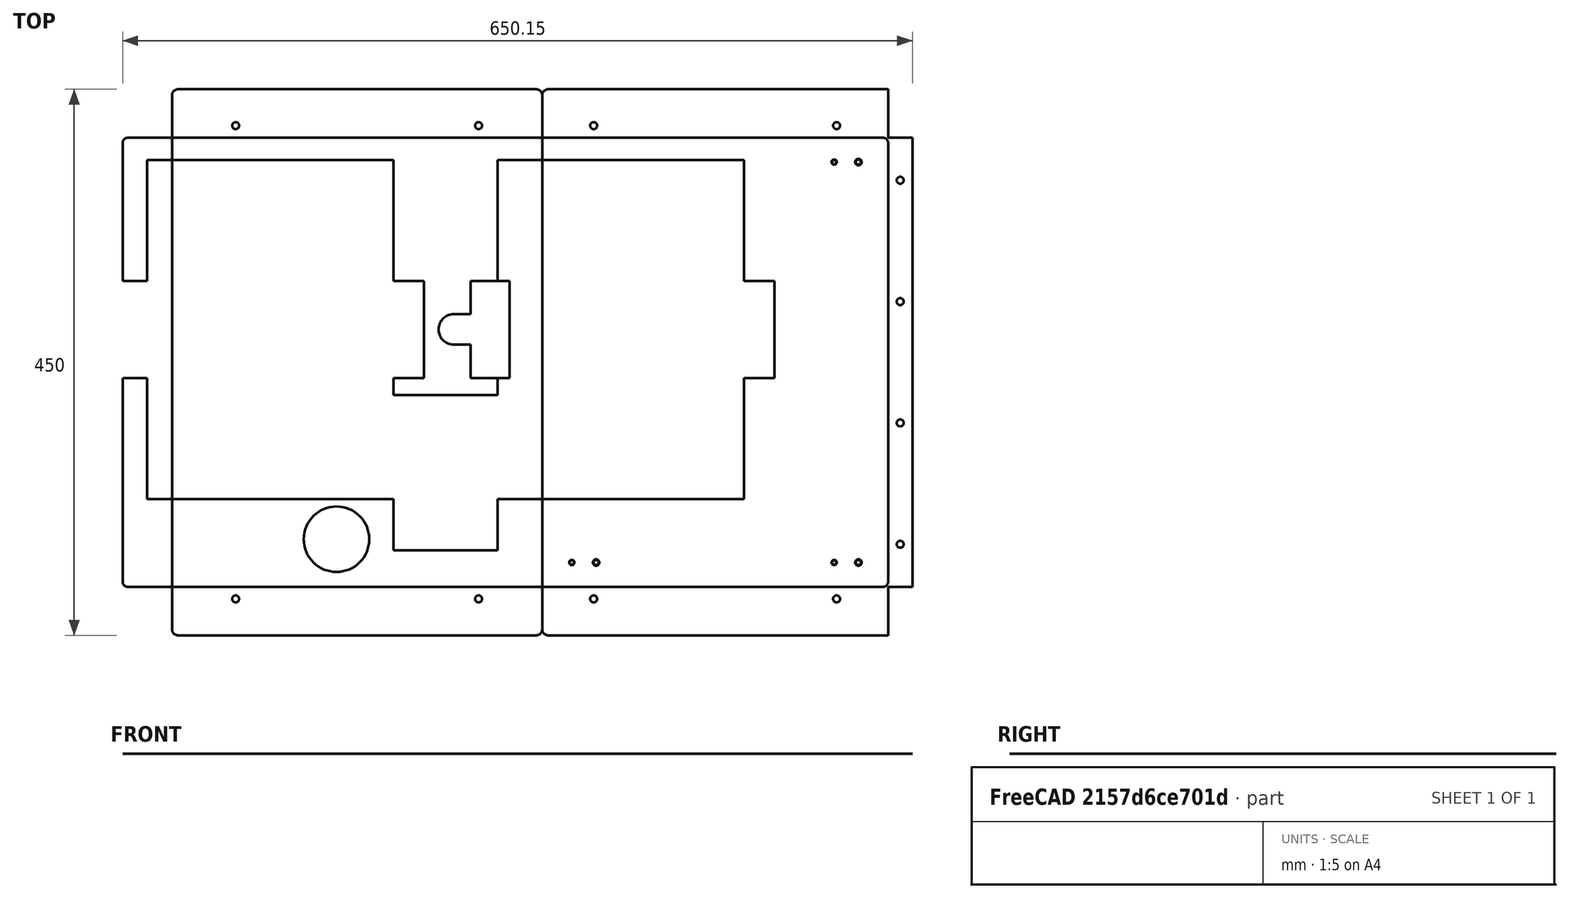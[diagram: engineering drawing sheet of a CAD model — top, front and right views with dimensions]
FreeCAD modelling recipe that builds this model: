
FCSTD DOCUMENT  (FreeCAD 0.18R14715 (Git))
Label: worksurface
License: All rights reserved
LicenseURL: http://en.wikipedia.org/wiki/All_rights_reserved
objects: Part::Feature×5, App::DocumentObjectGroup×5, Part::Part2DObjectPython×4, Spreadsheet::Sheet×1, App::FeaturePython×1, Part::FeaturePython×1
note: 10 computed .brp shape members not serialized (recipe doc carries the construction recipe); baked Part::Feature solids carry a one-line shape summary decoded from their .brp

FEATURE [Spreadsheet::Sheet] Spreadsheet  label="params"
  cells = A1=Name; B1=Value; C1=Notes; A2=sheet_width; B2(sheet_width)==12in; A3=sheet_length; B3(sheet_length)==24in; A4=y_rail_length; B4(y_rail_length)==370mm; A5=extrusion_unit_width; B5(extrusion_unit_width)==20mm; A6=mounting_hole_diam; B6(mounting_hole_diam)==5.75mm; A7=x_rail_hole_spacing; B7(x_rail_hole_spacing)==200mm; A8=y_rail_hole_spacing; B8(y_rail_hole_spacing)==100mm; A9=holes_offset_by; B9(holes_offset_by)==0mm; C9=It seems I made a mistake when this seemed nonzero earlier.; A10=x_rail_length; B10(x_rail_length)==1120mm; A11=flyplate_length; B11(flyplate_length)==85.5mm; A12=flyplate_height; B12(flyplate_height)==128mm; A13=morgue_diam; B13(morgue_diam)==54mm; C13=Smaller part of petri dish. Scintillation vial won't work, because it's too tall, at least with my current (alternate) Z-slides.; A14=dsub_height; B14(dsub_height)==32mm; C14=Adds a significant amount of space so you can grab it through the hole with your fingers.; A15=dsub_length; B15(dsub_length)==80mm; A16=chamber_bottom_to_dsub_mid; B16(chamber_bottom_to_dsub_mid)==6mm; C16=Clearance needs to account for PCB holes being offset a little from bottom, depending on chamber version.; A17=alignment_plate_min_thickness; B17(alignment_plate_min_thickness)==12.199999999999999mm; C17=So guide acrylic doesn't break so easily.  Divided total remaining space by 3.; A18=v1_chamber_length; B18(v1_chamber_length)==279.39999999999998mm; C18=TODO make above clearance larger if I have space; A19=v1_chamber_height; B19(v1_chamber_height)==203mm; A20=v1_nub_length; B20(v1_nub_length)==80mm; C20=Centered on chamber.; A21=v1_nub_height; B21(v1_nub_height)==25mm; C21=TODO how to accomodate both chambers? just use nub on top for v1? possible?; A22=v2_chamber_length; B22(v2_chamber_length)==279.39999999999998mm; C22=v2 chamber doesn't have the motor mounting nub v1 has.; A23=v2_chamber_height; B23(v2_chamber_height)==203mm; A24=cable_passthru_diam; B24(cable_passthru_diam)==25mm; C24=TODO have everything automatically evenly spaced (& automatically put as many flyplates in as possible?); A25=dsub_to_passthru; B25(dsub_to_passthru)==30mm; C25=Kind of long, so I hopefully won't have to bend cable too much when (dis)connecting.; C26=TODO flyplate orientation marks? minimum clearance for auto number as above; A27=primary_alignment_hole_diam; B27(primary_alignment_hole_diam)==0.13600000000000001in; A28=secondary_alignment_hole_diam; B28(secondary_alignment_hole_diam)==4.2000000000000002mm; C28=TODO how to basically make array of 3 of something, on a (right) triangle?; A29=primary_alignment_hole_upper_diam; B29(primary_alignment_hole_upper_diam)==4.2999999999999998mm; C29=Measured at bottom of taper pin (widest part).; A30=secondary_alignment_hole_upper_diam; B30(secondary_alignment_hole_upper_diam)==5.2999999999999998mm; C31=TODO TODO passthroughs for flow from below; C32=TODO TODO make space for more behavior chambers, and just support mounting onto multiple slats below?; C33=TODO TODO TODO consider reorienting chamber chambers,  particularly if doing above, to pack more in; C34=TODO how many cable passthroughs do I want?; A35=workspace_min_vac_x; B35(workspace_min_vac_x)==13cm; C35=Counting from top right corner (homing zero corner), on the inside of the vertical. Eyeballed.; A36=workspace_min_vac_y; B36(workspace_min_vac_y)==10cm; A37=chamber_top_to_closest_door_center_x; B37(chamber_top_to_closest_door_center_x)==15.35mm; C37=Y dimension in LibreCAD chamber drawing, but X dimension here since it's rotated. Not counting nub.; A38=chamber_edge_to_closest_door_center_y; B38(chamber_edge_to_closest_door_center_y)==126.697mm; C38=This is the 2nd closest door center in X, since which side of the midline the doors are on alternates, and the 1st is on the right.; A39=pcb_beyond_chamber_bottom; B39(pcb_beyond_chamber_bottom)==15.5mm; C39=And if horizontal, the D-Sub connector will extend beyond this. The pcb fits within v1 nub on top.; A40=part_manip_limit_clearance; B40(part_manip_limit_clearance)==4mm; A41=workspace_bottom_clearance; B41(workspace_bottom_clearance)==70mm; C41=Closest we want to drive effectors to their max Y, to avoid strain on cables and tubes, where max is defined as effectors in line with bottom edge of rail here.
FEATURE [Part::Part2DObjectPython] Rectangle001  label="vertical_space"  # Draft 2D object (typed FeaturePython)
  ChamferSize = 0
  Columns = 1
  FilletRadius = 0
  Height = 40
  Length = 20
  MakeFace = false
  Placement = pos=(284.8,0,0) rot=(0,0,1;0rad)
  Rows = 1
  expr: Length = params.extrusion_unit_width
  expr: Height = 2 * params.extrusion_unit_width
  expr: Placement.Base.x = params.sheet_width - vertical_space.Length
FEATURE [Part::Part2DObjectPython] Circle003  label="surface_mount_hole"  # Draft 2D object (typed FeaturePython)
  FirstAngle = 0
  LastAngle = 0
  MakeFace = false
  Radius = 2.875
  expr: Radius = params.mounting_hole_diam / 2
FEATURE [Part::Feature] Face  label="v1_nub_face"
  shape: bbox 80 x 25 x 2e-07 mm, 1 faces, 0 solids (baked)
FEATURE [Part::Feature] Face001  label="chamber_space_face"
  shape: bbox 279.4 x 203 x 2e-07 mm, 1 faces, 0 solids (baked)
FEATURE [Part::Part2DObjectPython] Fusion  label="all_chamber_space"  # Draft 2D object (typed FeaturePython)
  Base = -> Face001
  ChamferSize = 0
  Closed = false
  End = (228,99.7,0)
  FilletRadius = 0
  Length = 0
  MakeFace = true
  Placement = pos=(-357,-45.6,0) rot=(0,0,-1;1.5708rad)
  Points = (8) [(-225.3,585,0),(-225.3,560,0),(-325,560,0),(-325,357,0),(-45.6,357,0),(-45.6,560,0),(-145.3,560,0),(-145.3,585,0)]
  Start = (228,179.7,0)
  Subdivisions = 0
  Tool = -> Face
  expr: Placement.Base.x = -357mm
FEATURE [App::FeaturePython] dLabel  label="effector_limit"  # WARN: FeaturePython — macro-defined, semantics opaque (R4)
  CustomText = Part manipulator vac. limit
  LabelType = 0
  Placement = pos=(654.8,357,0) rot=(0,0,1;0rad)
  Points = (3) [(654.8,357,0),(655.8,357,0),(154.8,310,0)]
  StraightDirection = 0
  StraightDistance = 1
  TargetPoint = (154.8,310,0)
  Text = Part manipulator vac. limit
  expr: Placement.Base.x = effector_limit.TargetPoint.x + 500
  expr: TargetPoint.y = (2 * params.extrusion_unit_width + params.y_rail_length - params.workspace_min_vac_y) / 1mm
  expr: TargetPoint.x = (params.sheet_width - params.extrusion_unit_width - params.workspace_min_vac_x) / 1mm
FEATURE [App::DocumentObjectGroup] Group001  label="center_worksurface"
FEATURE [App::DocumentObjectGroup] Group003  label="upper_alignment_holes"
FEATURE [App::DocumentObjectGroup] Group004  label="lower_alignment_holes"
FEATURE [Part::FeaturePython] Clone001  label="alignment_plate_dsub_passthru"  # WARN: FeaturePython — macro-defined, semantics opaque (R4)
  AttacherType = Attacher::AttachEngine3D
  Fuse = false
  Scale = (1,1,1)
FEATURE [App::DocumentObjectGroup] Group002  label="alignment_plate"
  Group = -> [Group003,Clone001,Fusion]
FEATURE [Part::Part2DObjectPython] Circle015  label="surface_mount_hole_copy"  # Draft 2D object (typed FeaturePython)
  FirstAngle = 0
  LastAngle = 0
  MakeFace = false
  Radius = 2.875
  expr: Radius = params.mounting_hole_diam / 2
FEATURE [App::DocumentObjectGroup] Group  label="end_worksurface"
  Group = -> [Group004,Circle015]
FEATURE [Part::Feature] Subtraction002  label="alignment_plate_f"
  shape: bbox 630.2 x 370 x 2e-07 mm, 1 faces, 0 solids (baked)
FEATURE [Part::Feature] Subtraction  label="center_worksurface_f"
  shape: bbox 304.8 x 450 x 2e-07 mm, 1 faces, 0 solids (baked)
FEATURE [Part::Feature] Subtraction003  label="end_worksurface_f"
  shape: bbox 304.8 x 450 x 2e-07 mm, 1 faces, 0 solids (baked)
